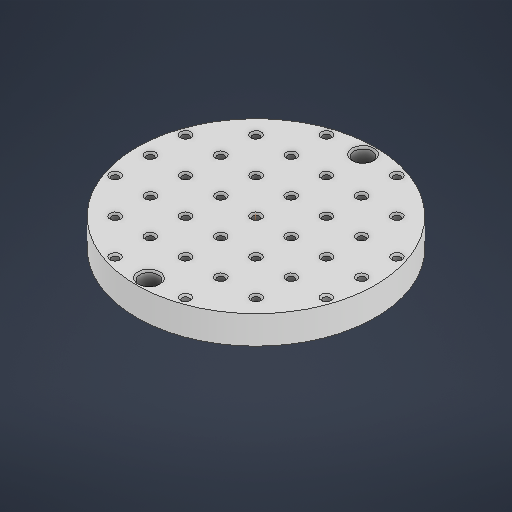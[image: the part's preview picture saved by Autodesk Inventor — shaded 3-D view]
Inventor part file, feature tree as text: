
AUTODESK INVENTOR PART (.ipt)
format: ipt  version: 2025 (Build 290162000, 162)  size: 317,952 bytes
history: native  units: in
note: dims shown in document units (in); Inventor stores cm internally (conversion verified against a paired STEP export)
features: sketch x6, extrude x3, other x1, hole x1, chamfer x1
ambient origin geometry x8: Origin, YZ Plane, XZ Plane, XY Plane, X Axis, Y Axis, Z Axis, Center Point
bodies: Solid1 (feature_tree)
feature tree (12):
  extrude  "Extrusion1"  Depth=0.7874in TaperAngle=0.0deg
  sketch  "Sketch2"  dims[d5=0.5118in d6=0.2264in]
  extrude  "Extrusion2"  Depth=0.5118in
  extrude  "Extrusion3"  Depth=0.2264in
  other  "Work Axis1"
  hole  "Hole1"  [1 undecoded]
  chamfer  "Chamfer2"  Distance=0.4724in
  sketch  "Sketch1"  dims[d0=6.6732in d1=0.7874in d2=0.0in]
  sketch  "Sketch3"  dims[d16=0.2362in]
  sketch  "Sketch Rectangular Pattern1"  dims[d3=5.9843in d4=0.5118in]
  sketch  "Sketch Rectangular Pattern2"  dims[d7=0.2264in d8=0.0in d9=0.0in d10=0.4724in d11=0.0in]
  sketch  "Sketch Rectangular Pattern3"  dims[d17=1.1811in d19=0.9843in d20=1.1811in d22=0.9843in d25=0.1936in d26=0.5906in d27=0.2756in d28=0.0787in d29=90.0deg d30=0.5906in d31=0.8108in d32=0.7874in d34=0.9843in d35=1.1811in d37=0.9843in d40=1.1811in d42=0.9843in d43=0.7874in d45=0.9843in d51=0.0492in d52=0.0787in d53=45.0deg]
note: 1 required parameter value undecoded (feature->parameter linkage not recoverable at this tier; creation-order binding heuristic only, values carry confidence <= 0.55)
